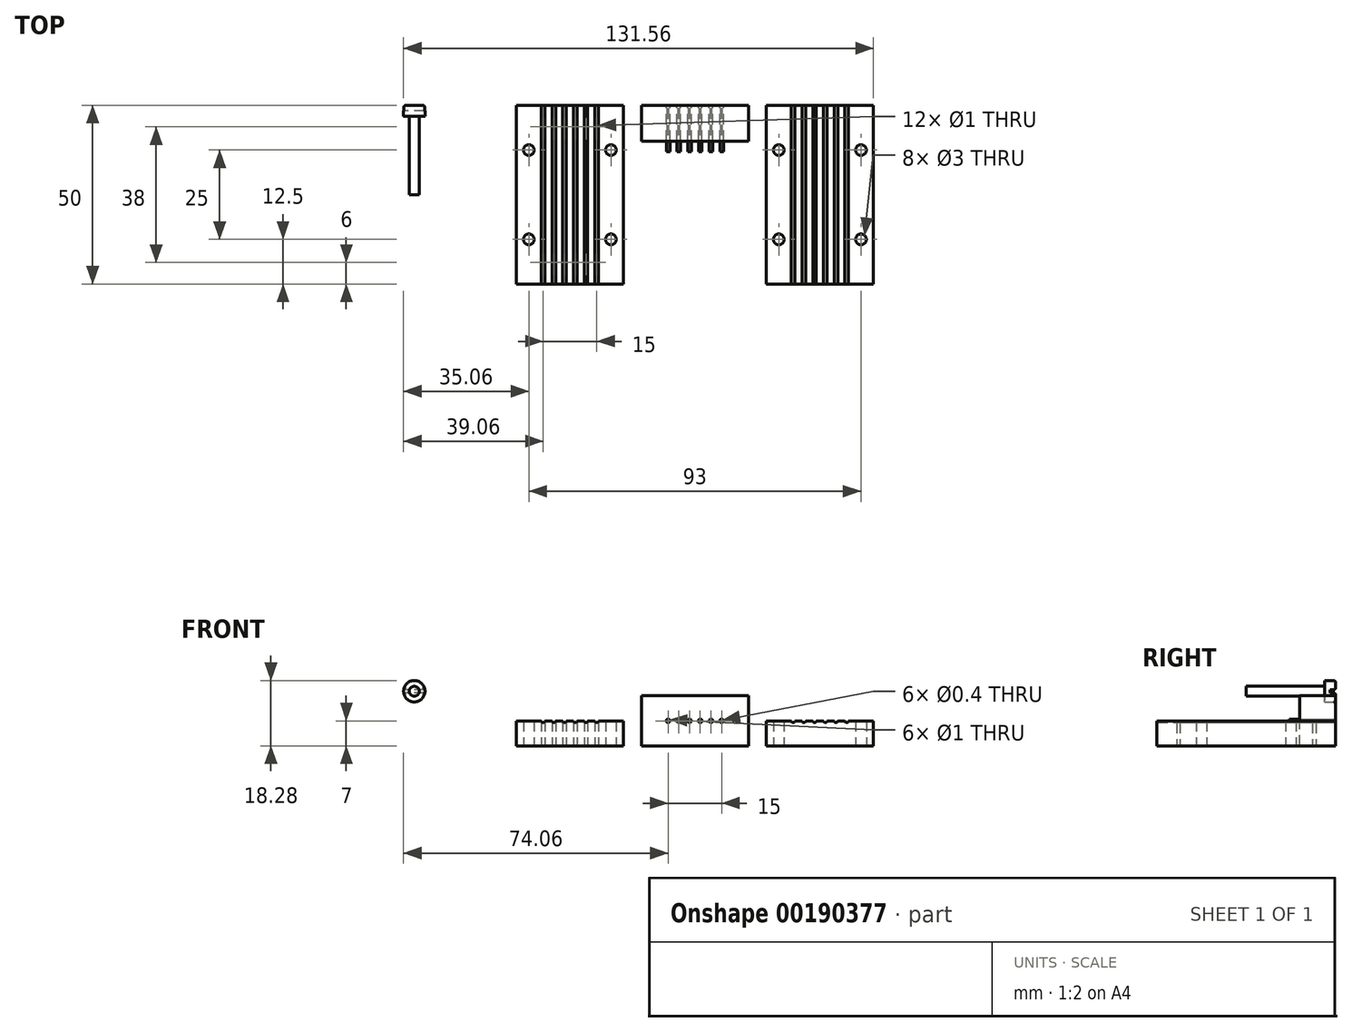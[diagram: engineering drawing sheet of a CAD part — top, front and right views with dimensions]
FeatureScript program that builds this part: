
annotation { "Feature Type Name" : "Feature", "Feature Type Description" : "" }
export const myFeature = defineFeature(function(context is Context, id is Id, definition is map)
    precondition{}
    {
        {
            var Q0;
            Q0=qCreatedBy(makeId("Front.planeOp"),FACE);
            var sketch = newSketch(context, id + "F0", { "sketchPlane" : qUnion([Q0])});
            skLineSegment(sketch, "E0.bottom", {"start": v(0, 0) * mm, "end": v(30, 0) * mm});
            skLineSegment(sketch, "E0.top", {"start": v(0, 7) * mm, "end": v(30, 7) * mm});
            skLineSegment(sketch, "E0.left", {"start": v(0, 0) * mm, "end": v(0, 7) * mm});
            skLineSegment(sketch, "E0.right", {"start": v(30, 0) * mm, "end": v(30, 7) * mm});
            skCircle(sketch, "E1", {"center": v(7.5, 7) * mm, "radius": 0.5 * mm});
            skCircle(sketch, "E2.1.0.0", {"center": v(10.5, 7) * mm, "radius": 0.5 * mm});
            skCircle(sketch, "E2.2.0.0", {"center": v(13.5, 7) * mm, "radius": 0.5 * mm});
            skCircle(sketch, "E2.3.0.0", {"center": v(16.5, 7) * mm, "radius": 0.5 * mm});
            skLineSegment(sketch, "E2.direction1", {"start": v(7.5, 7) * mm, "end": v(10.5, 7) * mm, "construction": true});
            skCircle(sketch, "E3.0.4.0", {"center": v(19.5, 7) * mm, "radius": 0.5 * mm});
            skCircle(sketch, "E3.0.5.0", {"center": v(22.5, 7) * mm, "radius": 0.5 * mm});
            skSolve(sketch);
        }
        {
            var Q0;
            Q0=makeQuery(id+"F0.imprint","IMPRINT",FACE,{"disambiguationData":[TD([[makeQuery(id+"F0.imprint","IMPRINT",EDGE,{"derivedFrom":sQuery(id+"F0.wireOp",EDGE,"E0.bottom")}),1.0]])]});
            extrude(context, id + "F1", {"entities" : qUnion([Q0]), "depth" : 50 * mm});
        }
        {
            var Q0;
            Q0=qCreatedBy(makeId("Front.planeOp"),FACE);
            var sketch = newSketch(context, id + "F2", { "sketchPlane" : qUnion([Q0])});
            skLineSegment(sketch, "E4.bottom", {"start": v(35, 0) * mm, "end": v(65, 0) * mm});
            skLineSegment(sketch, "E4.top", {"start": v(35, 7) * mm, "end": v(65, 7) * mm, "construction": true});
            skLineSegment(sketch, "E4.left", {"start": v(35, 0) * mm, "end": v(35, 7) * mm});
            skLineSegment(sketch, "E4.right", {"start": v(65, 0) * mm, "end": v(65, 7) * mm});
            skCircle(sketch, "E5", {"center": v(42.5, 7) * mm, "radius": 0.5 * mm});
            skCircle(sketch, "E6.1.0.0", {"center": v(45.5, 7) * mm, "radius": 0.5 * mm});
            skCircle(sketch, "E6.2.0.0", {"center": v(48.5, 7) * mm, "radius": 0.5 * mm});
            skCircle(sketch, "E6.3.0.0", {"center": v(51.5, 7) * mm, "radius": 0.5 * mm});
            skLineSegment(sketch, "E6.direction1", {"start": v(42.5, 7) * mm, "end": v(45.5, 7) * mm, "construction": true});
            skLineSegment(sketch, "E7.top", {"start": v(35, 14) * mm, "end": v(65, 14) * mm});
            skLineSegment(sketch, "E7.left", {"start": v(35, 0) * mm, "end": v(35, 14) * mm});
            skLineSegment(sketch, "E7.right", {"start": v(65, 0) * mm, "end": v(65, 14) * mm});
            skCircle(sketch, "E8", {"center": v(42.5, 7) * mm, "radius": 0.2 * mm});
            skCircle(sketch, "E9.1.0.0", {"center": v(45.5, 7) * mm, "radius": 0.2 * mm});
            skCircle(sketch, "E9.2.0.0", {"center": v(48.5, 7) * mm, "radius": 0.2 * mm});
            skCircle(sketch, "E9.3.0.0", {"center": v(51.5, 7) * mm, "radius": 0.2 * mm});
            skCircle(sketch, "E10.0.4.0", {"center": v(54.5, 7) * mm, "radius": 0.2 * mm});
            skCircle(sketch, "E10.0.5.0", {"center": v(57.5, 7) * mm, "radius": 0.2 * mm});
            skCircle(sketch, "E11.0.4.0", {"center": v(54.5, 7) * mm, "radius": 0.5 * mm});
            skCircle(sketch, "E11.0.5.0", {"center": v(57.5, 7) * mm, "radius": 0.5 * mm});
            skSolve(sketch);
        }
        {
            var Q0;
            Q0=makeQuery(id+"F2.imprint","IMPRINT",FACE,{"disambiguationData":[TD([[makeQuery(id+"F2.imprint","IMPRINT",EDGE,{"derivedFrom":sQuery(id+"F2.wireOp",EDGE,"E6.3.0.0")}),1.0]])]});
            var Q1;
            Q1=makeQuery(id+"F2.imprint","IMPRINT",FACE,{"disambiguationData":[TD([[makeQuery(id+"F2.imprint","IMPRINT",EDGE,{"derivedFrom":sQuery(id+"F2.wireOp",EDGE,"E6.2.0.0")}),1.0]])]});
            var Q2;
            Q2=makeQuery(id+"F2.imprint","IMPRINT",FACE,{"disambiguationData":[TD([[makeQuery(id+"F2.imprint","IMPRINT",EDGE,{"derivedFrom":sQuery(id+"F2.wireOp",EDGE,"E6.1.0.0")}),1.0]])]});
            var Q3;
            Q3=makeQuery(id+"F2.imprint","IMPRINT",FACE,{"disambiguationData":[TD([[makeQuery(id+"F2.imprint","IMPRINT",EDGE,{"derivedFrom":sQuery(id+"F2.wireOp",EDGE,"E5")}),1.0]])]});
            var Q4;
            Q4=makeQuery(id+"F2.imprint","IMPRINT",FACE,{"disambiguationData":[TD([[makeQuery(id+"F2.imprint","IMPRINT",EDGE,{"derivedFrom":sQuery(id+"F2.wireOp",EDGE,"E10.0.4.0")}),-1.0]])]});
            var Q5;
            Q5=makeQuery(id+"F2.imprint","IMPRINT",FACE,{"disambiguationData":[TD([[makeQuery(id+"F2.imprint","IMPRINT",EDGE,{"derivedFrom":sQuery(id+"F2.wireOp",EDGE,"E10.0.5.0")}),-1.0]])]});
            extrude(context, id + "F3", {"entities" : qUnion([Q0, Q1, Q2, Q3, Q4, Q5]), "depth" : 13 * mm});
        }
        {
            var Q0;
            Q0=makeQuery(id+"F2.imprint","IMPRINT",FACE,{"disambiguationData":[TD([[makeQuery(id+"F2.imprint","IMPRINT",EDGE,{"derivedFrom":sQuery(id+"F2.wireOp",EDGE,"E5")}),-1.0]])]});
            extrude(context, id + "F4", {"entities" : qUnion([Q0]), "depth" : 10 * mm});
        }
        {
            var Q0;
            Q0=qCreatedBy(makeId("Front.planeOp"),FACE);
            var sketch = newSketch(context, id + "F5", { "sketchPlane" : qUnion([Q0])});
            skCircle(sketch, "E12", {"center": v(-28.56, 15.28) * mm, "radius": 3 * mm});
            skCircle(sketch, "E13", {"center": v(-28.56, 15.28) * mm, "radius": 1.4 * mm});
            skSolve(sketch);
        }
        {
            var Q0;
            Q0=makeQuery(id+"F5.imprint","IMPRINT",FACE,{"disambiguationData":[TD([[makeQuery(id+"F5.imprint","IMPRINT",EDGE,{"derivedFrom":sQuery(id+"F5.wireOp",EDGE,"E12")}),1.0]])]});
            var Q1;
            Q1=makeQuery(id+"F5.imprint","IMPRINT",FACE,{"disambiguationData":[TD([[makeQuery(id+"F5.imprint","IMPRINT",EDGE,{"derivedFrom":sQuery(id+"F5.wireOp",EDGE,"E13")}),1.0]])]});
            extrude(context, id + "F6", {"entities" : qUnion([Q0, Q1]), "depth" : 3 * mm});
        }
        {
            var Q0;
            Q0=makeQuery(id+"F5.imprint","IMPRINT",FACE,{"disambiguationData":[TD([[makeQuery(id+"F5.imprint","IMPRINT",EDGE,{"derivedFrom":sQuery(id+"F5.wireOp",EDGE,"E13")}),1.0]])]});
            extrude(context, id + "F7", {"entities" : qUnion([Q0]), "operationType" : NewBodyOperationType.ADD, "depth" : 25 * mm});
        }
        {
            var Q0;
            Q0=makeQuery(id+"F5.imprint","IMPRINT",FACE,{"disambiguationData":[TD([[makeQuery(id+"F5.imprint","IMPRINT",EDGE,{"derivedFrom":sQuery(id+"F5.wireOp",EDGE,"E12")}),1.0]])]});
            var sketch = newSketch(context, id + "F8", { "sketchPlane" : qUnion([Q0])});
            skCircle(sketch, "E14.0", {"center": v(-28.56, 15.28) * mm, "radius": 1.4 * mm});
            skLineSegment(sketch, "E15.bottom", {"start": v(-24.57, 14.84) * mm, "end": v(-32.56, 14.84) * mm});
            skLineSegment(sketch, "E15.top", {"start": v(-24.57, 15.72) * mm, "end": v(-32.56, 15.72) * mm});
            skLineSegment(sketch, "E15.left", {"start": v(-24.57, 14.84) * mm, "end": v(-24.57, 15.72) * mm});
            skLineSegment(sketch, "E15.right", {"start": v(-32.56, 14.84) * mm, "end": v(-32.56, 15.72) * mm});
            skSolve(sketch);
        }
        {
            var Q0;
            {var subQ0=sQuery(id+"F8.wireOp",EDGE,"E15.top");var subQ1=sQuery(id+"F8.wireOp",EDGE,"E14.0");var subQ2=makeQuery(id+"F8.imprint","INTERSECT",VERTEX,{"disambiguationData":[OD(0.0)],"derivedFrom":[subQ1,subQ0]});Q0=makeQuery(id+"F8.imprint","IMPRINT",FACE,{"disambiguationData":[TD([[makeQuery(id+"F8.imprint","IMPRINT",EDGE,{"disambiguationData":[TD([[subQ2,-1.0]])],"derivedFrom":subQ1}),-1.0]])]});}
            var Q1;
            {var subQ0=sQuery(id+"F8.wireOp",EDGE,"E15.top");var subQ1=sQuery(id+"F8.wireOp",EDGE,"E14.0");var subQ2=makeQuery(id+"F8.imprint","INTERSECT",VERTEX,{"disambiguationData":[OD(0.0)],"derivedFrom":[subQ1,subQ0]});Q1=makeQuery(id+"F8.imprint","IMPRINT",FACE,{"disambiguationData":[TD([[makeQuery(id+"F8.imprint","IMPRINT",EDGE,{"disambiguationData":[TD([[subQ2,-1.0]])],"derivedFrom":subQ1}),1.0]])]});}
            var Q2;
            {var subQ0=sQuery(id+"F8.wireOp",EDGE,"E15.top");var subQ1=sQuery(id+"F8.wireOp",EDGE,"E14.0");var subQ2=makeQuery(id+"F8.imprint","INTERSECT",VERTEX,{"disambiguationData":[OD(1.0)],"derivedFrom":[subQ1,subQ0]});Q2=makeQuery(id+"F8.imprint","IMPRINT",FACE,{"disambiguationData":[TD([[makeQuery(id+"F8.imprint","IMPRINT",EDGE,{"disambiguationData":[TD([[subQ2,1.0]])],"derivedFrom":subQ1}),-1.0]])]});}
            extrude(context, id + "F9", {"entities" : qUnion([Q0, Q1, Q2]), "operationType" : NewBodyOperationType.REMOVE, "depth" : 1.5 * mm});
        }
        {
            var Q0;
            {var subQ0=sQuery(id+"F5.wireOp",EDGE,"E12");Q0=makeQuery(id+"F9.boolean.opBoolean","SPLIT",FACE,{"disambiguationData":[TD([makeQuery(id+"F9.opExtrude","SWEPT_FACE",FACE,{"disambiguationData":[OSD([sQuery(id+"F8.wireOp",EDGE,"E15.top")])]})])],"derivedFrom":makeQuery(id+"F6.opExtrude","CAP_FACE",FACE,{"disambiguationData":[OSD([subQ0])],"isStart":true})});}
            var Q1;
            {var subQ0=sQuery(id+"F5.wireOp",EDGE,"E12");Q1=makeQuery(id+"F9.boolean.opBoolean","SPLIT",FACE,{"disambiguationData":[TD([makeQuery(id+"F9.opExtrude","SWEPT_FACE",FACE,{"disambiguationData":[OSD([sQuery(id+"F8.wireOp",EDGE,"E15.bottom")])]})])],"derivedFrom":makeQuery(id+"F6.opExtrude","CAP_FACE",FACE,{"disambiguationData":[OSD([subQ0])],"isStart":true})});}
            fillet(context, id + "F10", {"entities" : qUnion([Q0, Q1]), "radius" : .5 * mm, "tangentPropagation" : true, "allowEdgeOverflow" : false});
        }
        {
            var Q0;
            Q0=makeQuery(id+"F1.opExtrude","SWEPT_FACE",FACE,{"disambiguationData":[OSD([sQuery(id+"F0.wireOp",EDGE,"E0.bottom")])]});
            var sketch = newSketch(context, id + "F11", { "sketchPlane" : qUnion([Q0])});
            skLineSegment(sketch, "E16", {"start": v(30, 50) * mm, "end": v(0, 0) * mm, "construction": true});
            skLineSegment(sketch, "E17.bottom", {"start": v(26.5, 37.5) * mm, "end": v(3.5, 37.5) * mm, "construction": true});
            skLineSegment(sketch, "E17.top", {"start": v(26.5, 12.5) * mm, "end": v(3.5, 12.5) * mm, "construction": true});
            skLineSegment(sketch, "E17.left", {"start": v(26.5, 37.5) * mm, "end": v(26.5, 12.5) * mm, "construction": true});
            skLineSegment(sketch, "E17.right", {"start": v(3.5, 37.5) * mm, "end": v(3.5, 12.5) * mm, "construction": true});
            skPoint(sketch, "E17.middle", {"position": v(15, 25) * mm});
            skCircle(sketch, "E18", {"center": v(3.5, 12.5) * mm, "radius": 1.5 * mm});
            skCircle(sketch, "E19.0.1.0", {"center": v(3.5, 37.5) * mm, "radius": 1.5 * mm});
            skCircle(sketch, "E19.1.0.0", {"center": v(26.5, 12.5) * mm, "radius": 1.5 * mm});
            skCircle(sketch, "E19.1.1.0", {"center": v(26.5, 37.5) * mm, "radius": 1.5 * mm});
            skLineSegment(sketch, "E19.direction1", {"start": v(3.5, 12.5) * mm, "end": v(26.5, 12.5) * mm, "construction": true});
            skLineSegment(sketch, "E19.direction2", {"start": v(3.5, 12.5) * mm, "end": v(3.5, 37.5) * mm, "construction": true});
            skLineSegment(sketch, "E20.bottom", {"start": v(22.5, 44) * mm, "end": v(7.5, 44) * mm, "construction": true});
            skLineSegment(sketch, "E20.top", {"start": v(22.5, 6) * mm, "end": v(7.5, 6) * mm, "construction": true});
            skLineSegment(sketch, "E20.left", {"start": v(22.5, 44) * mm, "end": v(22.5, 6) * mm, "construction": true});
            skLineSegment(sketch, "E20.right", {"start": v(7.5, 44) * mm, "end": v(7.5, 6) * mm, "construction": true});
            skCircle(sketch, "E21", {"center": v(7.5, 6) * mm, "radius": 0.5 * mm});
            skCircle(sketch, "E22.0.1.0", {"center": v(7.5, 44) * mm, "radius": 0.5 * mm});
            skCircle(sketch, "E22.1.0.0", {"center": v(10.5, 6) * mm, "radius": 0.5 * mm});
            skCircle(sketch, "E22.1.1.0", {"center": v(10.5, 44) * mm, "radius": 0.5 * mm});
            skCircle(sketch, "E22.2.0.0", {"center": v(13.5, 6) * mm, "radius": 0.5 * mm});
            skCircle(sketch, "E22.2.1.0", {"center": v(13.5, 44) * mm, "radius": 0.5 * mm});
            skCircle(sketch, "E22.3.0.0", {"center": v(16.5, 6) * mm, "radius": 0.5 * mm});
            skCircle(sketch, "E22.3.1.0", {"center": v(16.5, 44) * mm, "radius": 0.5 * mm});
            skLineSegment(sketch, "E22.direction1", {"start": v(7.5, 6) * mm, "end": v(10.5, 6) * mm, "construction": true});
            skLineSegment(sketch, "E22.direction2", {"start": v(7.5, 6) * mm, "end": v(7.5, 44) * mm, "construction": true});
            skCircle(sketch, "E23.0.4.0", {"center": v(19.5, 6) * mm, "radius": 0.5 * mm});
            skCircle(sketch, "E23.0.4.1", {"center": v(19.5, 44) * mm, "radius": 0.5 * mm});
            skCircle(sketch, "E23.0.5.0", {"center": v(22.5, 6) * mm, "radius": 0.5 * mm});
            skCircle(sketch, "E23.0.5.1", {"center": v(22.5, 44) * mm, "radius": 0.5 * mm});
            skSolve(sketch);
        }
        {
            var Q0;
            Q0=makeQuery(id+"F1.opExtrude","SWEPT_BODY",BODY,{"disambiguationData":[OSD([sQuery(id+"F0.wireOp",EDGE,"E0.bottom"),sQuery(id+"F0.wireOp",EDGE,"E0.top"),sQuery(id+"F0.wireOp",EDGE,"E0.left"),sQuery(id+"F0.wireOp",EDGE,"E0.right"),sQuery(id+"F0.wireOp",EDGE,"E1"),sQuery(id+"F0.wireOp",EDGE,"E2.1.0.0"),sQuery(id+"F0.wireOp",EDGE,"E2.2.0.0"),sQuery(id+"F0.wireOp",EDGE,"E2.3.0.0")])]});
            transform(context, id + "F12", {"entities" : qUnion([Q0]), "transformType" : TransformType.TRANSLATION_3D, "dx" : 70 * mm, "dy" : 0 * mm, "dz" : 0 * mm, "makeCopy" : true});
        }
        {
            var Q0;
            Q0=qSketchRegion(id+"F11",true);
            extrude(context, id + "F13", {"entities" : qUnion([Q0]), "operationType" : NewBodyOperationType.REMOVE, "oppositeDirection" : true, "depth" : 25 * mm});
        }
        {
            var Q0;
            Q0=makeQuery(id+"F12.opPattern","COPY",FACE,{"derivedFrom":makeQuery(id+"F1.opExtrude","SWEPT_FACE",FACE,{"disambiguationData":[OSD([sQuery(id+"F0.wireOp",EDGE,"E0.bottom")])]}),"instanceName":"1"});
            var sketch = newSketch(context, id + "F14", { "sketchPlane" : qUnion([Q0])});
            skLineSegment(sketch, "E24", {"start": v(70, 0) * mm, "end": v(100, 50) * mm, "construction": true});
            skLineSegment(sketch, "E25.bottom", {"start": v(73.5, 12.5) * mm, "end": v(96.5, 12.5) * mm, "construction": true});
            skLineSegment(sketch, "E25.top", {"start": v(73.5, 37.5) * mm, "end": v(96.5, 37.5) * mm, "construction": true});
            skLineSegment(sketch, "E25.left", {"start": v(73.5, 12.5) * mm, "end": v(73.5, 37.5) * mm, "construction": true});
            skLineSegment(sketch, "E25.right", {"start": v(96.5, 12.5) * mm, "end": v(96.5, 37.5) * mm, "construction": true});
            skPoint(sketch, "E25.middle", {"position": v(85, 25) * mm});
            skCircle(sketch, "E26", {"center": v(96.5, 37.5) * mm, "radius": 1.5 * mm});
            skCircle(sketch, "E27.0.1.0", {"center": v(96.5, 12.5) * mm, "radius": 1.5 * mm});
            skCircle(sketch, "E27.1.0.0", {"center": v(73.5, 37.5) * mm, "radius": 1.5 * mm});
            skCircle(sketch, "E27.1.1.0", {"center": v(73.5, 12.5) * mm, "radius": 1.5 * mm});
            skLineSegment(sketch, "E27.direction1", {"start": v(96.5, 37.5) * mm, "end": v(73.5, 37.5) * mm, "construction": true});
            skLineSegment(sketch, "E27.direction2", {"start": v(96.5, 37.5) * mm, "end": v(96.5, 12.5) * mm, "construction": true});
            skSolve(sketch);
        }
        {
            var Q0;
            Q0=qSketchRegion(id+"F14",true);
            extrude(context, id + "F15", {"entities" : qUnion([Q0]), "operationType" : NewBodyOperationType.REMOVE, "oppositeDirection" : true, "depth" : 25 * mm});
        }
    });
